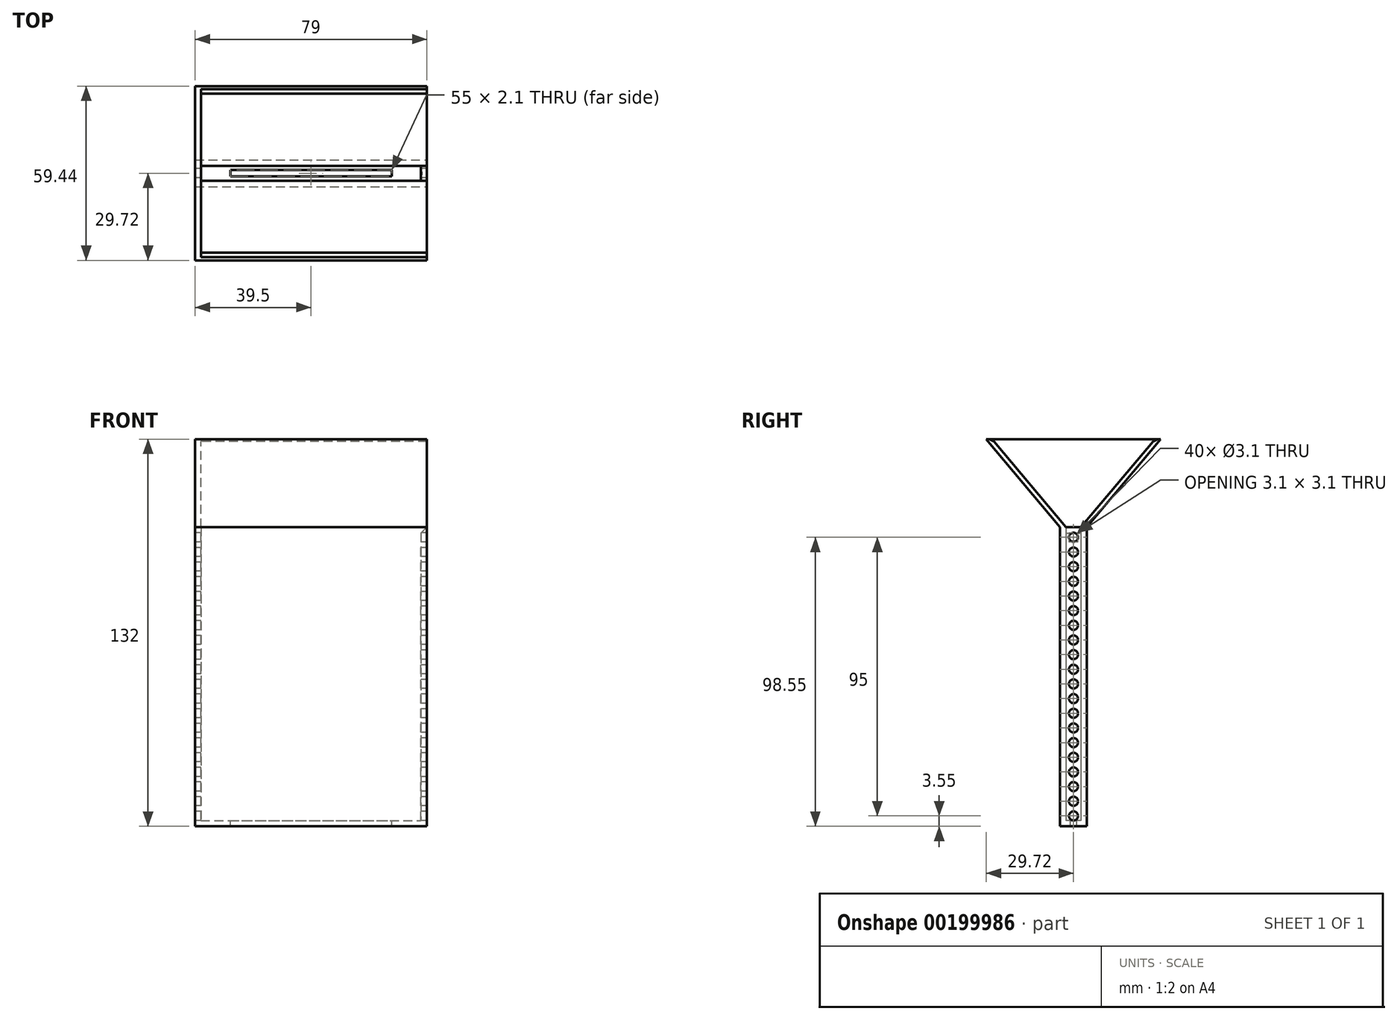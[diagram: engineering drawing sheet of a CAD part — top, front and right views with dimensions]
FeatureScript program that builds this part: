
annotation { "Feature Type Name" : "Feature", "Feature Type Description" : "" }
export const myFeature = defineFeature(function(context is Context, id is Id, definition is map)
    precondition{}
    {
        {
            var Q0;
            Q0=qCreatedBy(makeId("Top.planeOp"),FACE);
            var sketch = newSketch(context, id + "F0", { "sketchPlane" : qUnion([Q0])});
            skLineSegment(sketch, "E0.bottom", {"start": v(-39.5, 4.55) * mm, "end": v(39.5, 4.55) * mm});
            skLineSegment(sketch, "E0.top", {"start": v(-39.5, -4.55) * mm, "end": v(39.5, -4.55) * mm});
            skLineSegment(sketch, "E0.left", {"start": v(-39.5, 4.55) * mm, "end": v(-39.5, -4.55) * mm});
            skLineSegment(sketch, "E0.right", {"start": v(39.5, 4.55) * mm, "end": v(39.5, -4.55) * mm});
            skPoint(sketch, "E0.middle", {"position": v(0, 0) * mm});
            skLineSegment(sketch, "E1.bottom", {"start": v(-37.5, 2.55) * mm, "end": v(37.5, 2.55) * mm});
            skLineSegment(sketch, "E1.top", {"start": v(-37.5, -2.55) * mm, "end": v(37.5, -2.55) * mm});
            skLineSegment(sketch, "E1.left", {"start": v(-37.5, 2.55) * mm, "end": v(-37.5, -2.55) * mm});
            skLineSegment(sketch, "E1.right", {"start": v(37.5, 2.55) * mm, "end": v(37.5, -2.55) * mm});
            skLineSegment(sketch, "E2.bottom", {"start": v(-27.5, 1.05) * mm, "end": v(27.5, 1.05) * mm});
            skLineSegment(sketch, "E2.top", {"start": v(-27.5, -1.05) * mm, "end": v(27.5, -1.05) * mm});
            skLineSegment(sketch, "E2.left", {"start": v(-27.5, 1.05) * mm, "end": v(-27.5, -1.05) * mm});
            skLineSegment(sketch, "E2.right", {"start": v(27.5, 1.05) * mm, "end": v(27.5, -1.05) * mm});
            skSolve(sketch);
        }
        {
            var Q0;
            Q0=makeQuery(id+"F0.imprint","IMPRINT",FACE,{"disambiguationData":[TD([[makeQuery(id+"F0.imprint","IMPRINT",EDGE,{"derivedFrom":sQuery(id+"F0.wireOp",EDGE,"E0.bottom")}),-1.0]])]});
            extrude(context, id + "F1", {"entities" : qUnion([Q0]), "depth" : (5 * 20) * mm});
        }
        {
            var Q0;
            Q0=makeQuery(id+"F0.imprint","IMPRINT",FACE,{"disambiguationData":[TD([[makeQuery(id+"F0.imprint","IMPRINT",EDGE,{"derivedFrom":sQuery(id+"F0.wireOp",EDGE,"E1.bottom")}),-1.0]])]});
            var Q1;
            Q1=makeQuery(id+"F0.imprint","IMPRINT",FACE,{"disambiguationData":[TD([[makeQuery(id+"F0.imprint","IMPRINT",EDGE,{"derivedFrom":sQuery(id+"F0.wireOp",EDGE,"E0.bottom")}),-1.0]])]});
            extrude(context, id + "F2", {"entities" : qUnion([Q0, Q1]), "operationType" : NewBodyOperationType.ADD, "oppositeDirection" : true, "depth" : 2 * mm});
        }
        {
            var Q0;
            {var subQ0=sQuery(id+"F0.wireOp",EDGE,"E0.left");Q0=makeQuery(id+"F2.boolean.opBoolean","MERGE",FACE,{"derivedFrom":[makeQuery(id+"F1.opExtrude","SWEPT_FACE",FACE,{"disambiguationData":[OSD([subQ0])]}),makeQuery(id+"F2.opExtrude","SWEPT_FACE",FACE,{"disambiguationData":[OSD([subQ0])]})]});}
            var sketch = newSketch(context, id + "F3", { "sketchPlane" : qUnion([Q0])});
            skLineSegment(sketch, "E3", {"start": v(0, -2) * mm, "end": v(0, 100) * mm, "construction": true});
            skCircle(sketch, "E4", {"center": v(0, 1.55) * mm, "radius": 1.55 * mm});
            skLineSegment(sketch, "E5.0", {"start": v(-1.05, 0) * mm, "end": v(1.05, 0) * mm});
            skCircle(sketch, "E6.0.1.0", {"center": v(0, 6.55) * mm, "radius": 1.55 * mm});
            skCircle(sketch, "E6.0.2.0", {"center": v(0, 11.55) * mm, "radius": 1.55 * mm});
            skCircle(sketch, "E6.0.3.0", {"center": v(0, 16.55) * mm, "radius": 1.55 * mm});
            skCircle(sketch, "E6.0.4.0", {"center": v(0, 21.55) * mm, "radius": 1.55 * mm});
            skCircle(sketch, "E6.0.5.0", {"center": v(0, 26.55) * mm, "radius": 1.55 * mm});
            skCircle(sketch, "E6.0.6.0", {"center": v(0, 31.55) * mm, "radius": 1.55 * mm});
            skCircle(sketch, "E6.0.7.0", {"center": v(0, 36.55) * mm, "radius": 1.55 * mm});
            skCircle(sketch, "E6.0.8.0", {"center": v(0, 41.55) * mm, "radius": 1.55 * mm});
            skCircle(sketch, "E6.0.9.0", {"center": v(0, 46.55) * mm, "radius": 1.55 * mm});
            skCircle(sketch, "E6.0.10.0", {"center": v(0, 51.55) * mm, "radius": 1.55 * mm});
            skCircle(sketch, "E6.0.11.0", {"center": v(0, 56.55) * mm, "radius": 1.55 * mm});
            skCircle(sketch, "E6.0.12.0", {"center": v(0, 61.55) * mm, "radius": 1.55 * mm});
            skCircle(sketch, "E6.0.13.0", {"center": v(0, 66.55) * mm, "radius": 1.55 * mm});
            skCircle(sketch, "E6.0.14.0", {"center": v(0, 71.55) * mm, "radius": 1.55 * mm});
            skCircle(sketch, "E6.0.15.0", {"center": v(0, 76.55) * mm, "radius": 1.55 * mm});
            skCircle(sketch, "E6.0.16.0", {"center": v(0, 81.55) * mm, "radius": 1.55 * mm});
            skCircle(sketch, "E6.0.17.0", {"center": v(0, 86.55) * mm, "radius": 1.55 * mm});
            skCircle(sketch, "E6.0.18.0", {"center": v(0, 91.55) * mm, "radius": 1.55 * mm});
            skCircle(sketch, "E6.0.19.0", {"center": v(0, 96.55) * mm, "radius": 1.55 * mm});
            skLineSegment(sketch, "E6.direction1", {"start": v(0, 1.55) * mm, "end": v(25, 1.55) * mm, "construction": true});
            skLineSegment(sketch, "E6.direction2", {"start": v(0, 1.55) * mm, "end": v(0, 6.55) * mm, "construction": true});
            skSolve(sketch);
        }
        {
            var Q0;
            Q0 = qSketchRegion(id + "F3", true);
            extrude(context, id + "F4", {"entities" : qUnion([Q0]), "operationType" : NewBodyOperationType.REMOVE, "endBound" : BoundingType.THROUGH_ALL, "oppositeDirection" : true, "depth" : 25 * mm});
        }
        {
            var Q0;
            {var subQ0=sQuery(id+"F0.wireOp",EDGE,"E0.left");Q0=makeQuery(id+"F2.boolean.opBoolean","MERGE",FACE,{"derivedFrom":[makeQuery(id+"F1.opExtrude","SWEPT_FACE",FACE,{"disambiguationData":[OSD([subQ0])]}),makeQuery(id+"F2.opExtrude","SWEPT_FACE",FACE,{"disambiguationData":[OSD([subQ0])]})]});}
            var sketch = newSketch(context, id + "F5", { "sketchPlane" : qUnion([Q0])});
            skLineSegment(sketch, "E7.0", {"start": v(-4.55, 100) * mm, "end": v(4.55, 100) * mm});
            skLineSegment(sketch, "E8.0", {"start": v(-2.55, 100) * mm, "end": v(-2.55, 0) * mm});
            skLineSegment(sketch, "E9.0", {"start": v(2.55, 100) * mm, "end": v(2.55, 0) * mm});
            skLineSegment(sketch, "E10", {"start": v(-2.55, 100) * mm, "end": v(-27.72, 130) * mm});
            skLineSegment(sketch, "E11", {"start": v(-27.72, 130) * mm, "end": v(27.72, 130) * mm});
            skLineSegment(sketch, "E12", {"start": v(27.72, 130) * mm, "end": v(2.55, 100) * mm});
            skLineSegment(sketch, "E13", {"start": v(4.55, 100) * mm, "end": v(29.72, 130) * mm});
            skLineSegment(sketch, "E14", {"start": v(29.72, 130) * mm, "end": v(-29.72, 130) * mm});
            skLineSegment(sketch, "E15", {"start": v(-29.72, 130) * mm, "end": v(-4.55, 100) * mm});
            skSolve(sketch);
        }
        {
            var Q0;
            {var subQ4=sQuery(id+"F5.wireOp",EDGE,"E10");Q0=makeQuery(id+"F5.imprint","IMPRINT",FACE,{"disambiguationData":[TD([[makeQuery(id+"F5.imprint","IMPRINT",EDGE,{"derivedFrom":subQ4}),1.0]])]});}
            var Q1;
            {var subQ4=sQuery(id+"F5.wireOp",EDGE,"E12");Q1=makeQuery(id+"F5.imprint","IMPRINT",FACE,{"disambiguationData":[TD([[makeQuery(id+"F5.imprint","IMPRINT",EDGE,{"derivedFrom":subQ4}),1.0]])]});}
            var Q2;
            {var subQ0=sQuery(id+"F0.wireOp",EDGE,"E0.right");Q2=makeQuery(id+"F2.boolean.opBoolean","MERGE",FACE,{"derivedFrom":[makeQuery(id+"F1.opExtrude","SWEPT_FACE",FACE,{"disambiguationData":[OSD([subQ0])]}),makeQuery(id+"F2.opExtrude","SWEPT_FACE",FACE,{"disambiguationData":[OSD([subQ0])]})]});}
            var Q3;
            Q3=makeQuery(id+"F1.opExtrude","SWEPT_BODY",BODY,{"disambiguationData":[OSD([sQuery(id+"F0.wireOp",EDGE,"E0.bottom"),sQuery(id+"F0.wireOp",EDGE,"E0.top"),sQuery(id+"F0.wireOp",EDGE,"E0.left"),sQuery(id+"F0.wireOp",EDGE,"E0.right"),sQuery(id+"F0.wireOp",EDGE,"E1.bottom"),sQuery(id+"F0.wireOp",EDGE,"E1.top"),sQuery(id+"F0.wireOp",EDGE,"E1.left"),sQuery(id+"F0.wireOp",EDGE,"E1.right")])]});
            extrude(context, id + "F6", {"entities" : qUnion([Q0, Q1]), "operationType" : NewBodyOperationType.ADD, "endBound" : BoundingType.UP_TO_SURFACE, "oppositeDirection" : true, "endBoundEntityFace" : qUnion([Q2]), "endBoundEntityBody" : qUnion([Q3]), "depth" : 25 * mm});
        }
        {
            var Q0;
            {var subQ0=sQuery(id+"F5.wireOp",EDGE,"E10");Q0=makeQuery(id+"F5.imprint","IMPRINT",FACE,{"disambiguationData":[TD([[makeQuery(id+"F5.imprint","IMPRINT",EDGE,{"derivedFrom":subQ0}),-1.0]])]});}
            var Q1;
            Q1=makeQuery(id+"F1.opExtrude","SWEPT_FACE",FACE,{"disambiguationData":[OSD([sQuery(id+"F0.wireOp",EDGE,"E1.left")])]});
            extrude(context, id + "F7", {"entities" : qUnion([Q0]), "operationType" : NewBodyOperationType.ADD, "endBound" : BoundingType.UP_TO_SURFACE, "oppositeDirection" : true, "endBoundEntityFace" : qUnion([Q1]), "depth" : 25 * mm});
        }
        {
            var Q0;
            Q0=makeQuery(id+"F1.opExtrude","CAP_EDGE",EDGE,{"disambiguationData":[OSD([sQuery(id+"F0.wireOp",EDGE,"E1.right")])],"isStart":false});
            var Q1;
            Q1=makeQuery(id+"F7.opExtrude","CAP_EDGE",EDGE,{"disambiguationData":[OSD([sQuery(id+"F5.wireOp",EDGE,"E14")])],"isStart":false});
            var Q2;
            Q2=makeQuery(id+"F6.opExtrude","SWEPT_EDGE",EDGE,{"disambiguationData":[OSD([sQuery(id+"F5.wireOp",EDGE,"E12"),sQuery(id+"F5.wireOp",EDGE,"E14")])]});
            var Q3;
            Q3=makeQuery(id+"F6.opExtrude","SWEPT_EDGE",EDGE,{"disambiguationData":[OSD([sQuery(id+"F5.wireOp",EDGE,"E10"),sQuery(id+"F5.wireOp",EDGE,"E14")])]});
            chamfer(context, id + "F8", {"entities" : qUnion([Q0, Q1, Q2, Q3]), "width" : 2 * mm, "tangentPropagation" : true});
        }
    });
